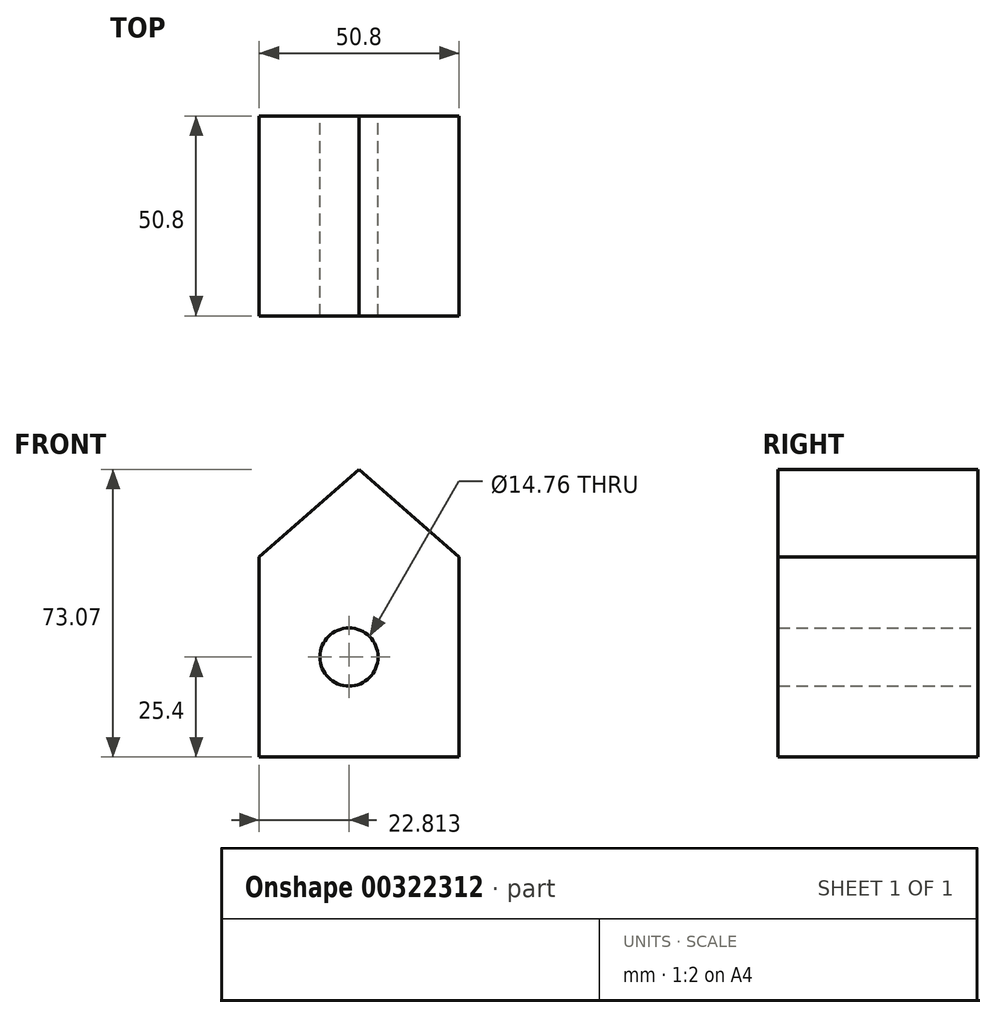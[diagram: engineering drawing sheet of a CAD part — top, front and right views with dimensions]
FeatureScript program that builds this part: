
annotation { "Feature Type Name" : "Feature", "Feature Type Description" : "" }
export const myFeature = defineFeature(function(context is Context, id is Id, definition is map)
    precondition{}
    {
        {
            var Q0;
            Q0=qCreatedBy(makeId("Front.planeOp"),FACE);
            var sketch = newSketch(context, id + "F0", { "sketchPlane" : qUnion([Q0])});
            skLineSegment(sketch, "E0.bottom", {"start": v(25.4, -25.4) * mm, "end": v(-25.4, -25.4) * mm});
            skLineSegment(sketch, "E0.left", {"start": v(25.4, -25.4) * mm, "end": v(25.4, 25.4) * mm});
            skLineSegment(sketch, "E0.right", {"start": v(-25.4, -25.4) * mm, "end": v(-25.4, 25.4) * mm});
            skPoint(sketch, "E0.middle", {"position": v(0, 0) * mm});
            skLineSegment(sketch, "E1", {"start": v(-25.4, 25.4) * mm, "end": v(0, 47.67) * mm});
            skLineSegment(sketch, "E2", {"start": v(0, 47.67) * mm, "end": v(25.4, 25.4) * mm});
            skCircle(sketch, "E3", {"center": v(-2.59, 0) * mm, "radius": 7.38 * mm});
            skSolve(sketch);
        }
        {
            var Q0;
            Q0=makeQuery(id+"F0.imprint","IMPRINT",FACE,{"disambiguationData":[TD([[makeQuery(id+"F0.imprint","IMPRINT",EDGE,{"derivedFrom":sQuery(id+"F0.wireOp",EDGE,"E0.bottom")}),-1.0]])]});
            extrude(context, id + "F1", {"entities" : qUnion([Q0]), "depth" : 50.8 * mm});
        }
    });
